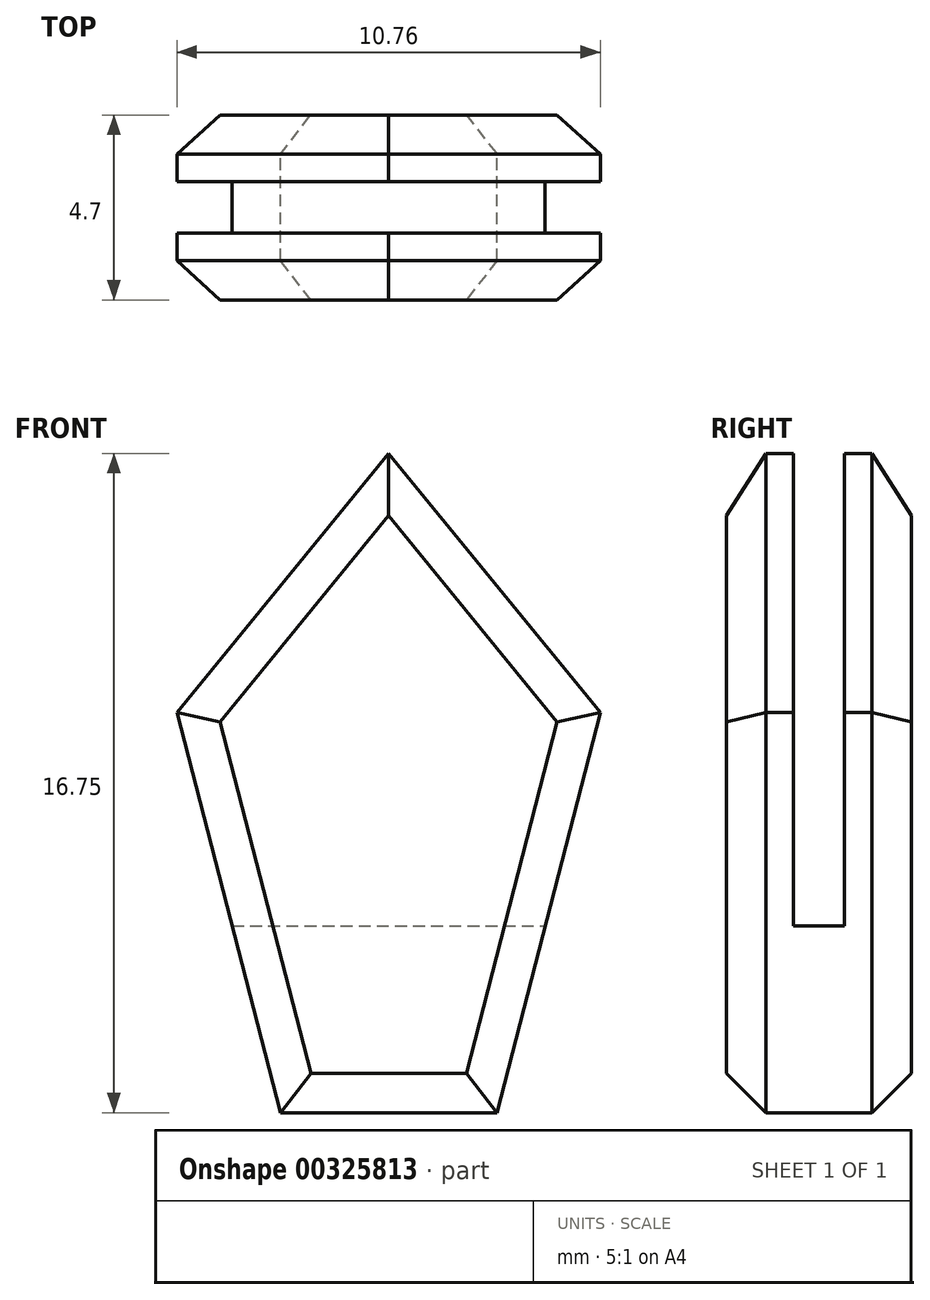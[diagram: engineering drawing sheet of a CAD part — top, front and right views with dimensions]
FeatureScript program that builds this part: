
annotation { "Feature Type Name" : "Feature", "Feature Type Description" : "" }
export const myFeature = defineFeature(function(context is Context, id is Id, definition is map)
    precondition{}
    {
        {
            var Q0;
            Q0=qCreatedBy(makeId("Front.planeOp"),FACE);
            var sketch = newSketch(context, id + "F0", { "sketchPlane" : qUnion([Q0])});
            skLineSegment(sketch, "E0", {"start": v(-2.75, 0) * mm, "end": v(2.75, 0) * mm});
            skLineSegment(sketch, "E1", {"start": v(-2.75, 0) * mm, "end": v(-5.38, 10.17) * mm});
            skLineSegment(sketch, "E2", {"start": v(2.75, 0) * mm, "end": v(5.38, 10.17) * mm});
            skLineSegment(sketch, "E3", {"start": v(5.38, 10.17) * mm, "end": v(0, 16.75) * mm});
            skLineSegment(sketch, "E4", {"start": v(0, 16.75) * mm, "end": v(-5.38, 10.17) * mm});
            skSolve(sketch);
        }
        {
            var Q0;
            Q0 = qSketchRegion(id + "F0", true);
            var Q1;
            Q1=makeQuery(id+"F0.imprint","IMPRINT",FACE,{"disambiguationData":[TD([[makeQuery(id+"F0.imprint","IMPRINT",EDGE,{"derivedFrom":sQuery(id+"F0.wireOp",EDGE,"E0")}),1.0]])]});
            extrude(context, id + "F1", {"entities" : qUnion([Q0, Q1]), "depth" : 4.7 * mm});
        }
        {
            var Q0;
            Q0=qCreatedBy(makeId("Right.planeOp"),FACE);
            var sketch = newSketch(context, id + "F2", { "sketchPlane" : qUnion([Q0])});
            skLineSegment(sketch, "E5.bottom", {"start": v(-3, 16.75) * mm, "end": v(-1.7, 16.75) * mm});
            skLineSegment(sketch, "E5.top", {"start": v(-3, 4.75) * mm, "end": v(-1.7, 4.75) * mm});
            skLineSegment(sketch, "E5.left", {"start": v(-3, 16.75) * mm, "end": v(-3, 4.75) * mm});
            skLineSegment(sketch, "E5.right", {"start": v(-1.7, 16.75) * mm, "end": v(-1.7, 4.75) * mm});
            skCircle(sketch, "E6", {"center": v(-2.35, 4.75) * mm, "radius": 2.35 * mm, "construction": true});
            skSolve(sketch);
        }
        {
            var Q0;
            Q0=makeQuery(id+"F2.imprint","IMPRINT",FACE,{"disambiguationData":[TD([[makeQuery(id+"F2.imprint","IMPRINT",EDGE,{"derivedFrom":sQuery(id+"F2.wireOp",EDGE,"E5.bottom")}),-1.0]])]});
            extrude(context, id + "F3", {"entities" : qUnion([Q0]), "operationType" : NewBodyOperationType.REMOVE, "endBound" : BoundingType.SYMMETRIC, "oppositeDirection" : true, "depth" : 20 * mm});
        }
        {
            var Q0;
            Q0=makeQuery(id+"F1.opExtrude","CAP_FACE",FACE,{"disambiguationData":[OSD([sQuery(id+"F0.wireOp",EDGE,"E0"),sQuery(id+"F0.wireOp",EDGE,"E1"),sQuery(id+"F0.wireOp",EDGE,"E2"),sQuery(id+"F0.wireOp",EDGE,"E3"),sQuery(id+"F0.wireOp",EDGE,"E4")])],"isStart":false});
            var Q1;
            Q1=makeQuery(id+"F1.opExtrude","CAP_FACE",FACE,{"disambiguationData":[OSD([sQuery(id+"F0.wireOp",EDGE,"E0"),sQuery(id+"F0.wireOp",EDGE,"E1"),sQuery(id+"F0.wireOp",EDGE,"E2"),sQuery(id+"F0.wireOp",EDGE,"E3"),sQuery(id+"F0.wireOp",EDGE,"E4")])],"isStart":true});
            chamfer(context, id + "F4", {"entities" : qUnion([Q0, Q1]), "width" : 1 * mm, "tangentPropagation" : true});
        }
    });
